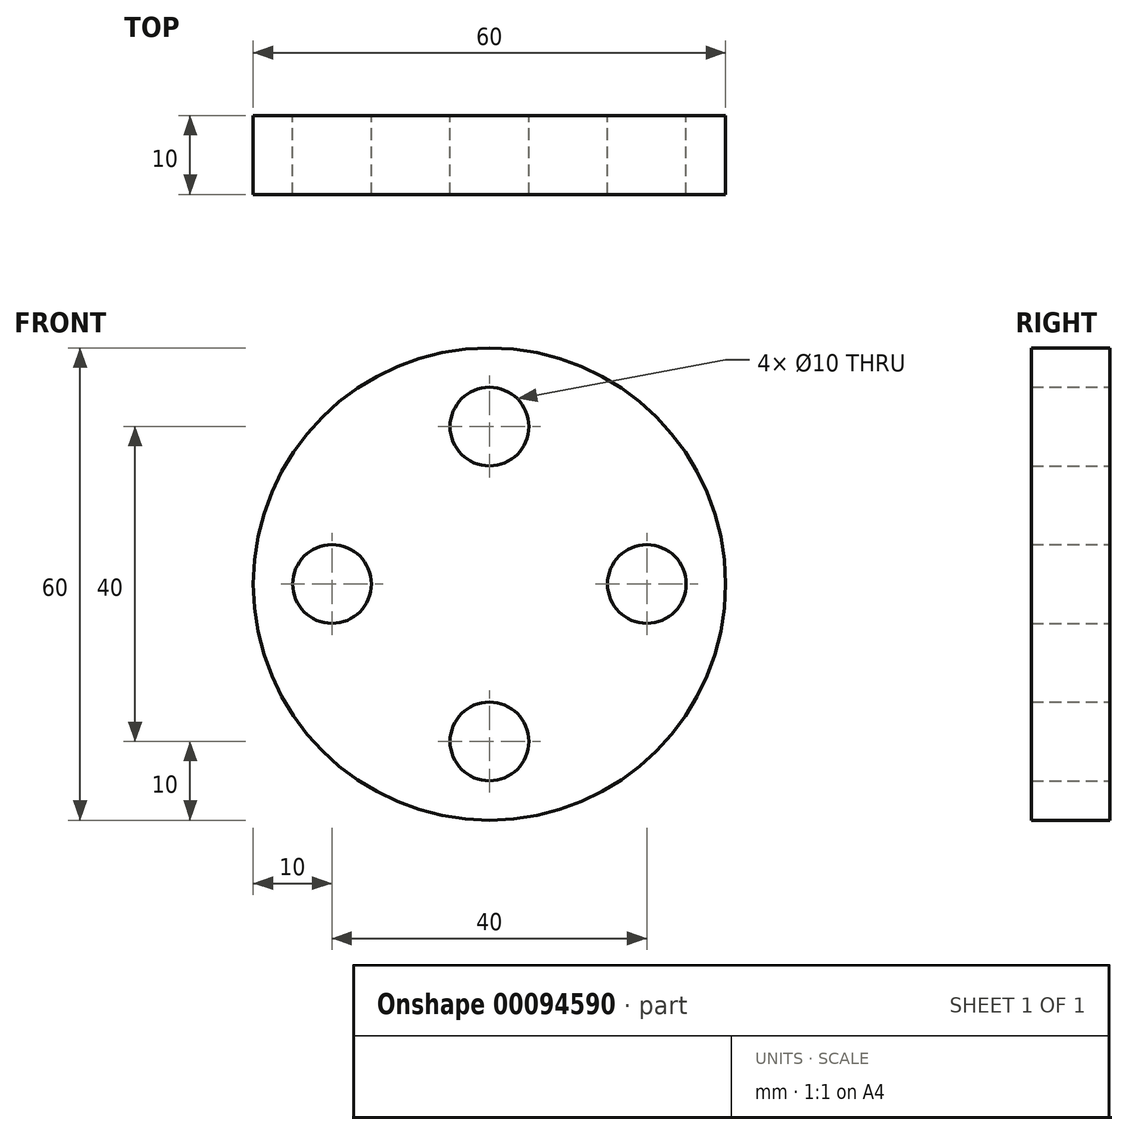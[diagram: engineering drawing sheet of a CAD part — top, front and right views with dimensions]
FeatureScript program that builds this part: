
annotation { "Feature Type Name" : "Feature", "Feature Type Description" : "" }
export const myFeature = defineFeature(function(context is Context, id is Id, definition is map)
    precondition{}
    {
        {
            var Q0;
            Q0=qCreatedBy(makeId("Front.planeOp"),FACE);
            var sketch = newSketch(context, id + "F0", { "sketchPlane" : qUnion([Q0])});
            skCircle(sketch, "E0", {"center": v(0, 0) * mm, "radius": 30 * mm});
            skCircle(sketch, "E1", {"center": v(0, 0) * mm, "radius": 20 * mm, "construction": true});
            skLineSegment(sketch, "E2", {"start": v(0, -30) * mm, "end": v(0, 30) * mm, "construction": true});
            skLineSegment(sketch, "E3", {"start": v(-30, 0) * mm, "end": v(30, 0) * mm, "construction": true});
            skCircle(sketch, "E4", {"center": v(-20, 0) * mm, "radius": 5 * mm});
            skCircle(sketch, "E5.1.0", {"center": v(0, -20) * mm, "radius": 5 * mm});
            skCircle(sketch, "E5.2.0", {"center": v(20, 0) * mm, "radius": 5 * mm});
            skCircle(sketch, "E5.3.0", {"center": v(0, 20) * mm, "radius": 5 * mm});
            skLineSegment(sketch, "E5.anchor1", {"start": v(0, 0) * mm, "end": v(-20, 0) * mm, "construction": true});
            skLineSegment(sketch, "E5.anchor2", {"start": v(0, 0) * mm, "end": v(0, 20) * mm, "construction": true});
            skSolve(sketch);
        }
        {
            var Q0;
            Q0=makeQuery(id+"F0.imprint","IMPRINT",FACE,{"disambiguationData":[TD([[makeQuery(id+"F0.imprint","IMPRINT",EDGE,{"derivedFrom":sQuery(id+"F0.wireOp",EDGE,"E0")}),1.0]])]});
            extrude(context, id + "F1", {"entities" : qUnion([Q0]), "depth" : 10 * mm});
        }
    });
